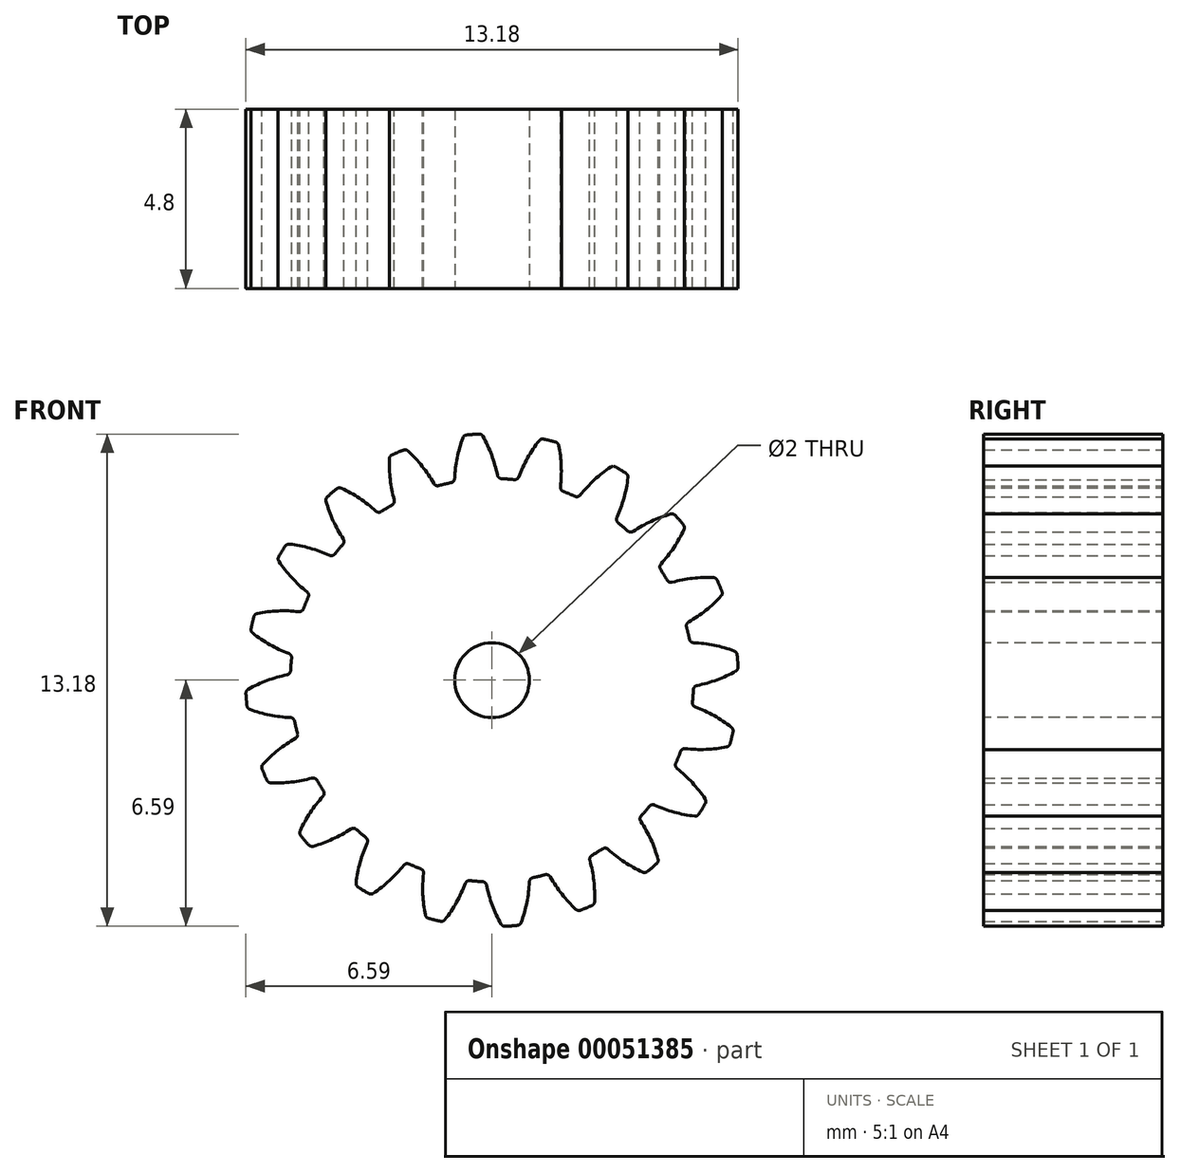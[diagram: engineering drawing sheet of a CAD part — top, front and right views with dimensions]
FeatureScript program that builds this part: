
annotation { "Feature Type Name" : "Feature", "Feature Type Description" : "" }
export const myFeature = defineFeature(function(context is Context, id is Id, definition is map)
    precondition{}
    {
        {
            var Q0;
            Q0=qCreatedBy(makeId("Front.planeOp"),FACE);
            var sketch = newSketch(context, id + "F0", { "sketchPlane" : qUnion([Q0])});
            skCircle(sketch, "E0", {"center": v(0, 0) * mm, "radius": 6 * mm, "construction": true});
            skCircle(sketch, "E1", {"center": v(0, 0) * mm, "radius": 5.4 * mm, "construction": true});
            skCircle(sketch, "E2", {"center": v(0, 0) * mm, "radius": 6.6 * mm, "construction": true});
            skLineSegment(sketch, "E3", {"start": v(0, 0) * mm, "end": v(0, 7.77) * mm, "construction": true});
            skPoint(sketch, "E4", {"position": v(0, 6) * mm});
            skLineSegment(sketch, "E5", {"start": v(0, 6) * mm, "end": v(-7.8, 6) * mm, "construction": true});
            skCircle(sketch, "E6.cCircle", {"center": v(0, 0) * mm, "radius": 7.77 * mm, "construction": true});
            skLineSegment(sketch, "E6.0", {"start": v(-0.61, 7.77) * mm, "end": v(0.61, 7.77) * mm, "construction": true});
            skLineSegment(sketch, "E6.1", {"start": v(0.61, 7.77) * mm, "end": v(1.82, 7.58) * mm, "construction": true});
            skLineSegment(sketch, "E6.2", {"start": v(1.82, 7.58) * mm, "end": v(2.98, 7.2) * mm, "construction": true});
            skLineSegment(sketch, "E6.3", {"start": v(2.98, 7.2) * mm, "end": v(4.07, 6.65) * mm, "construction": true});
            skLineSegment(sketch, "E6.4", {"start": v(4.07, 6.65) * mm, "end": v(5.06, 5.93) * mm, "construction": true});
            skLineSegment(sketch, "E6.5", {"start": v(5.06, 5.93) * mm, "end": v(5.93, 5.06) * mm, "construction": true});
            skLineSegment(sketch, "E6.6", {"start": v(5.93, 5.06) * mm, "end": v(6.65, 4.07) * mm, "construction": true});
            skLineSegment(sketch, "E6.7", {"start": v(6.65, 4.07) * mm, "end": v(7.2, 2.98) * mm, "construction": true});
            skLineSegment(sketch, "E6.8", {"start": v(7.2, 2.98) * mm, "end": v(7.58, 1.82) * mm, "construction": true});
            skLineSegment(sketch, "E6.9", {"start": v(7.58, 1.82) * mm, "end": v(7.77, 0.61) * mm, "construction": true});
            skLineSegment(sketch, "E6.10", {"start": v(7.77, 0.61) * mm, "end": v(7.77, -0.61) * mm, "construction": true});
            skLineSegment(sketch, "E6.11", {"start": v(7.77, -0.61) * mm, "end": v(7.58, -1.82) * mm, "construction": true});
            skLineSegment(sketch, "E6.12", {"start": v(7.58, -1.82) * mm, "end": v(7.2, -2.98) * mm, "construction": true});
            skLineSegment(sketch, "E6.13", {"start": v(7.2, -2.98) * mm, "end": v(6.65, -4.07) * mm, "construction": true});
            skLineSegment(sketch, "E6.14", {"start": v(6.65, -4.07) * mm, "end": v(5.93, -5.06) * mm, "construction": true});
            skLineSegment(sketch, "E6.15", {"start": v(5.93, -5.06) * mm, "end": v(5.06, -5.93) * mm, "construction": true});
            skLineSegment(sketch, "E6.16", {"start": v(5.06, -5.93) * mm, "end": v(4.07, -6.65) * mm, "construction": true});
            skLineSegment(sketch, "E6.17", {"start": v(4.07, -6.65) * mm, "end": v(2.98, -7.2) * mm, "construction": true});
            skLineSegment(sketch, "E6.18", {"start": v(2.98, -7.2) * mm, "end": v(1.82, -7.58) * mm, "construction": true});
            skLineSegment(sketch, "E6.19", {"start": v(1.82, -7.58) * mm, "end": v(0.61, -7.77) * mm, "construction": true});
            skLineSegment(sketch, "E6.20", {"start": v(0.61, -7.77) * mm, "end": v(-0.61, -7.77) * mm, "construction": true});
            skLineSegment(sketch, "E6.21", {"start": v(-0.61, -7.77) * mm, "end": v(-1.82, -7.58) * mm, "construction": true});
            skLineSegment(sketch, "E6.22", {"start": v(-1.82, -7.58) * mm, "end": v(-2.98, -7.2) * mm, "construction": true});
            skLineSegment(sketch, "E6.23", {"start": v(-2.98, -7.2) * mm, "end": v(-4.07, -6.65) * mm, "construction": true});
            skLineSegment(sketch, "E6.24", {"start": v(-4.07, -6.65) * mm, "end": v(-5.06, -5.93) * mm, "construction": true});
            skLineSegment(sketch, "E6.25", {"start": v(-5.06, -5.93) * mm, "end": v(-5.93, -5.06) * mm, "construction": true});
            skLineSegment(sketch, "E6.26", {"start": v(-5.93, -5.06) * mm, "end": v(-6.65, -4.07) * mm, "construction": true});
            skLineSegment(sketch, "E6.27", {"start": v(-6.65, -4.07) * mm, "end": v(-7.2, -2.98) * mm, "construction": true});
            skLineSegment(sketch, "E6.28", {"start": v(-7.2, -2.98) * mm, "end": v(-7.58, -1.82) * mm, "construction": true});
            skLineSegment(sketch, "E6.29", {"start": v(-7.58, -1.82) * mm, "end": v(-7.77, -0.61) * mm, "construction": true});
            skLineSegment(sketch, "E6.30", {"start": v(-7.77, -0.61) * mm, "end": v(-7.77, 0.61) * mm, "construction": true});
            skLineSegment(sketch, "E6.31", {"start": v(-7.77, 0.61) * mm, "end": v(-7.58, 1.82) * mm, "construction": true});
            skLineSegment(sketch, "E6.32", {"start": v(-7.58, 1.82) * mm, "end": v(-7.2, 2.98) * mm, "construction": true});
            skLineSegment(sketch, "E6.33", {"start": v(-7.2, 2.98) * mm, "end": v(-6.65, 4.07) * mm, "construction": true});
            skLineSegment(sketch, "E6.34", {"start": v(-6.65, 4.07) * mm, "end": v(-5.93, 5.06) * mm, "construction": true});
            skLineSegment(sketch, "E6.35", {"start": v(-5.93, 5.06) * mm, "end": v(-5.06, 5.93) * mm, "construction": true});
            skLineSegment(sketch, "E6.36", {"start": v(-5.06, 5.93) * mm, "end": v(-4.07, 6.65) * mm, "construction": true});
            skLineSegment(sketch, "E6.37", {"start": v(-4.07, 6.65) * mm, "end": v(-2.98, 7.2) * mm, "construction": true});
            skLineSegment(sketch, "E6.38", {"start": v(-2.98, 7.2) * mm, "end": v(-1.82, 7.58) * mm, "construction": true});
            skLineSegment(sketch, "E6.39", {"start": v(-1.82, 7.58) * mm, "end": v(-0.61, 7.77) * mm, "construction": true});
            skPoint(sketch, "E6.0.midPoint", {"position": v(0, 7.77) * mm});
            skLineSegment(sketch, "E7.0", {"start": v(0, 7.77) * mm, "end": v(1.22, 7.68) * mm, "construction": true});
            skLineSegment(sketch, "E7.1", {"start": v(1.22, 7.68) * mm, "end": v(2.4, 7.4) * mm, "construction": true});
            skLineSegment(sketch, "E7.2", {"start": v(2.4, 7.4) * mm, "end": v(3.53, 6.93) * mm, "construction": true});
            skLineSegment(sketch, "E7.3", {"start": v(3.53, 6.93) * mm, "end": v(4.57, 6.29) * mm, "construction": true});
            skLineSegment(sketch, "E7.4", {"start": v(4.57, 6.29) * mm, "end": v(5.5, 5.5) * mm, "construction": true});
            skLineSegment(sketch, "E7.5", {"start": v(5.5, 5.5) * mm, "end": v(6.29, 4.57) * mm, "construction": true});
            skLineSegment(sketch, "E7.6", {"start": v(6.29, 4.57) * mm, "end": v(6.93, 3.53) * mm, "construction": true});
            skLineSegment(sketch, "E7.7", {"start": v(6.93, 3.53) * mm, "end": v(7.4, 2.4) * mm, "construction": true});
            skLineSegment(sketch, "E7.8", {"start": v(7.4, 2.4) * mm, "end": v(7.68, 1.22) * mm, "construction": true});
            skLineSegment(sketch, "E7.9", {"start": v(7.68, 1.22) * mm, "end": v(7.77, 0) * mm, "construction": true});
            skLineSegment(sketch, "E7.10", {"start": v(7.77, 0) * mm, "end": v(7.68, -1.22) * mm, "construction": true});
            skLineSegment(sketch, "E7.11", {"start": v(7.68, -1.22) * mm, "end": v(7.4, -2.4) * mm, "construction": true});
            skLineSegment(sketch, "E7.12", {"start": v(7.4, -2.4) * mm, "end": v(6.93, -3.53) * mm, "construction": true});
            skLineSegment(sketch, "E7.13", {"start": v(6.93, -3.53) * mm, "end": v(6.29, -4.57) * mm, "construction": true});
            skLineSegment(sketch, "E7.14", {"start": v(6.29, -4.57) * mm, "end": v(5.5, -5.5) * mm, "construction": true});
            skLineSegment(sketch, "E7.15", {"start": v(5.5, -5.5) * mm, "end": v(4.57, -6.29) * mm, "construction": true});
            skLineSegment(sketch, "E7.16", {"start": v(4.57, -6.29) * mm, "end": v(3.53, -6.93) * mm, "construction": true});
            skLineSegment(sketch, "E7.17", {"start": v(3.53, -6.93) * mm, "end": v(2.4, -7.4) * mm, "construction": true});
            skLineSegment(sketch, "E7.18", {"start": v(2.4, -7.4) * mm, "end": v(1.22, -7.68) * mm, "construction": true});
            skLineSegment(sketch, "E7.19", {"start": v(1.22, -7.68) * mm, "end": v(0, -7.77) * mm, "construction": true});
            skLineSegment(sketch, "E7.20", {"start": v(0, -7.77) * mm, "end": v(-1.22, -7.68) * mm, "construction": true});
            skLineSegment(sketch, "E7.21", {"start": v(-1.22, -7.68) * mm, "end": v(-2.4, -7.4) * mm, "construction": true});
            skLineSegment(sketch, "E7.22", {"start": v(-2.4, -7.4) * mm, "end": v(-3.53, -6.93) * mm, "construction": true});
            skLineSegment(sketch, "E7.23", {"start": v(-3.53, -6.93) * mm, "end": v(-4.57, -6.29) * mm, "construction": true});
            skLineSegment(sketch, "E7.24", {"start": v(-4.57, -6.29) * mm, "end": v(-5.5, -5.5) * mm, "construction": true});
            skLineSegment(sketch, "E7.25", {"start": v(-5.5, -5.5) * mm, "end": v(-6.29, -4.57) * mm, "construction": true});
            skLineSegment(sketch, "E7.26", {"start": v(-6.29, -4.57) * mm, "end": v(-6.93, -3.53) * mm, "construction": true});
            skLineSegment(sketch, "E7.27", {"start": v(-6.93, -3.53) * mm, "end": v(-7.4, -2.4) * mm, "construction": true});
            skLineSegment(sketch, "E7.28", {"start": v(-7.4, -2.4) * mm, "end": v(-7.68, -1.22) * mm, "construction": true});
            skLineSegment(sketch, "E7.29", {"start": v(-7.68, -1.22) * mm, "end": v(-7.77, 0) * mm, "construction": true});
            skLineSegment(sketch, "E7.30", {"start": v(-7.77, 0) * mm, "end": v(-7.68, 1.22) * mm, "construction": true});
            skLineSegment(sketch, "E7.31", {"start": v(-7.68, 1.22) * mm, "end": v(-7.4, 2.4) * mm, "construction": true});
            skLineSegment(sketch, "E7.32", {"start": v(-7.4, 2.4) * mm, "end": v(-6.93, 3.53) * mm, "construction": true});
            skLineSegment(sketch, "E7.33", {"start": v(-6.93, 3.53) * mm, "end": v(-6.29, 4.57) * mm, "construction": true});
            skLineSegment(sketch, "E7.34", {"start": v(-6.29, 4.57) * mm, "end": v(-5.5, 5.5) * mm, "construction": true});
            skLineSegment(sketch, "E7.35", {"start": v(-5.5, 5.5) * mm, "end": v(-4.57, 6.29) * mm, "construction": true});
            skLineSegment(sketch, "E7.36", {"start": v(-4.57, 6.29) * mm, "end": v(-3.53, 6.93) * mm, "construction": true});
            skLineSegment(sketch, "E7.37", {"start": v(-3.53, 6.93) * mm, "end": v(-2.4, 7.4) * mm, "construction": true});
            skLineSegment(sketch, "E7.38", {"start": v(-2.4, 7.4) * mm, "end": v(-1.22, 7.68) * mm, "construction": true});
            skLineSegment(sketch, "E7.39", {"start": v(-1.22, 7.68) * mm, "end": v(0, 7.77) * mm, "construction": true});
            skLineSegment(sketch, "E8", {"start": v(0, 0) * mm, "end": v(-0.61, 7.77) * mm, "construction": true});
            skLineSegment(sketch, "E9", {"start": v(0, 6) * mm, "end": v(-7.35, 3.32) * mm, "construction": true});
            skCircle(sketch, "E10", {"center": v(0, 6) * mm, "radius": 3.6 * mm, "construction": true});
            skPoint(sketch, "E11", {"position": v(-3.38, 4.77) * mm});
            skCircle(sketch, "E12", {"center": v(-3.38, 4.77) * mm, "radius": 3.6 * mm, "construction": true});
            skArc(sketch, "E13", {"start": v(-0.24, 6.53) * mm, "mid": v(0, 6.02) * mm, "end": v(0.14, 5.49) * mm});
            skArc(sketch, "E14.MirrorCS", {"start": v(-0.78, 6.49) * mm, "mid": v(-0.93, 5.95) * mm, "end": v(-1, 5.4) * mm});
            skArc(sketch, "E15", {"start": v(-0.68, 6.56) * mm, "mid": v(-0.52, 6.58) * mm, "end": v(-0.35, 6.6) * mm});
            skArc(sketch, "E16", {"start": v(-1.1, 5.29) * mm, "mid": v(0.42, -5.38) * mm, "end": v(0.26, 5.4) * mm});
            skPoint(sketch, "E17.visualSharp", {"position": v(-1, 5.3) * mm});
            skArc(sketch, "E17.filletArc", {"start": v(-1.1, 5.29) * mm, "mid": v(-1.03, 5.33) * mm, "end": v(-1, 5.4) * mm});
            skPoint(sketch, "E18.visualSharp", {"position": v(0.16, 5.4) * mm});
            skArc(sketch, "E18.filletArc", {"start": v(0.14, 5.49) * mm, "mid": v(0.18, 5.42) * mm, "end": v(0.26, 5.4) * mm});
            skPoint(sketch, "E19.visualSharp", {"position": v(-0.76, 6.56) * mm});
            skArc(sketch, "E19.filletArc", {"start": v(-0.68, 6.56) * mm, "mid": v(-0.74, 6.54) * mm, "end": v(-0.78, 6.49) * mm});
            skPoint(sketch, "E20.visualSharp", {"position": v(-0.28, 6.6) * mm});
            skArc(sketch, "E20.filletArc", {"start": v(-0.24, 6.53) * mm, "mid": v(-0.29, 6.58) * mm, "end": v(-0.35, 6.6) * mm});
            skLineSegment(sketch, "E21", {"start": v(0, 0) * mm, "end": v(-1.44, 6.92) * mm, "construction": true});
            skPoint(sketch, "E22.1.0", {"position": v(-1.51, 5.18) * mm});
            skPoint(sketch, "E22.1.1", {"position": v(-1.85, 5.7) * mm});
            skArc(sketch, "E22.1.2", {"start": v(-2.25, 6.13) * mm, "mid": v(-1.87, 5.73) * mm, "end": v(-1.56, 5.27) * mm});
            skArc(sketch, "E22.1.3", {"start": v(-2.68, 6.03) * mm, "mid": v(-2.53, 6.1) * mm, "end": v(-2.37, 6.16) * mm});
            skPoint(sketch, "E22.1.4", {"position": v(-2.3, 6.18) * mm});
            skPoint(sketch, "E22.1.5", {"position": v(-2.6, 4.74) * mm});
            skArc(sketch, "E22.1.6", {"start": v(-2.75, 5.93) * mm, "mid": v(-2.73, 5.37) * mm, "end": v(-2.62, 4.83) * mm});
            skPoint(sketch, "E22.1.7", {"position": v(-2.74, 6) * mm});
            skArc(sketch, "E22.1.8", {"start": v(-1.56, 5.27) * mm, "mid": v(-1.5, 5.21) * mm, "end": v(-1.42, 5.2) * mm});
            skArc(sketch, "E22.1.9", {"start": v(-2.68, 6.03) * mm, "mid": v(-2.73, 6) * mm, "end": v(-2.75, 5.93) * mm});
            skArc(sketch, "E22.1.10", {"start": v(-2.68, 4.69) * mm, "mid": v(-2.63, 4.75) * mm, "end": v(-2.62, 4.83) * mm});
            skArc(sketch, "E22.1.11", {"start": v(-2.25, 6.13) * mm, "mid": v(-2.3, 6.16) * mm, "end": v(-2.37, 6.16) * mm});
            skPoint(sketch, "E22.2.0", {"position": v(-3.04, 4.46) * mm});
            skPoint(sketch, "E22.2.1", {"position": v(-3.53, 4.85) * mm});
            skArc(sketch, "E22.2.2", {"start": v(-4.03, 5.14) * mm, "mid": v(-3.55, 4.87) * mm, "end": v(-3.11, 4.53) * mm});
            skArc(sketch, "E22.2.3", {"start": v(-4.4, 4.91) * mm, "mid": v(-4.29, 5.02) * mm, "end": v(-4.16, 5.12) * mm});
            skPoint(sketch, "E22.2.4", {"position": v(-4.1, 5.17) * mm});
            skPoint(sketch, "E22.2.5", {"position": v(-3.93, 3.7) * mm});
            skArc(sketch, "E22.2.6", {"start": v(-4.45, 4.79) * mm, "mid": v(-4.25, 4.27) * mm, "end": v(-3.98, 3.78) * mm});
            skPoint(sketch, "E22.2.7", {"position": v(-4.46, 4.86) * mm});
            skArc(sketch, "E22.2.8", {"start": v(-3.11, 4.53) * mm, "mid": v(-3.04, 4.5) * mm, "end": v(-2.96, 4.51) * mm});
            skArc(sketch, "E22.2.9", {"start": v(-4.4, 4.91) * mm, "mid": v(-4.45, 4.85) * mm, "end": v(-4.45, 4.79) * mm});
            skArc(sketch, "E22.2.10", {"start": v(-4, 3.63) * mm, "mid": v(-3.96, 3.7) * mm, "end": v(-3.98, 3.78) * mm});
            skArc(sketch, "E22.2.11", {"start": v(-4.03, 5.14) * mm, "mid": v(-4.1, 5.15) * mm, "end": v(-4.16, 5.12) * mm});
            skPoint(sketch, "E22.3.0", {"position": v(-4.27, 3.3) * mm});
            skPoint(sketch, "E22.3.1", {"position": v(-4.85, 3.53) * mm});
            skArc(sketch, "E22.3.2", {"start": v(-5.43, 3.64) * mm, "mid": v(-4.88, 3.53) * mm, "end": v(-4.36, 3.34) * mm});
            skArc(sketch, "E22.3.3", {"start": v(-5.71, 3.3) * mm, "mid": v(-5.63, 3.45) * mm, "end": v(-5.54, 3.59) * mm});
            skPoint(sketch, "E22.3.4", {"position": v(-5.5, 3.65) * mm});
            skPoint(sketch, "E22.3.5", {"position": v(-4.88, 2.3) * mm});
            skArc(sketch, "E22.3.6", {"start": v(-5.7, 3.18) * mm, "mid": v(-5.36, 2.74) * mm, "end": v(-4.96, 2.36) * mm});
            skPoint(sketch, "E22.3.7", {"position": v(-5.75, 3.24) * mm});
            skArc(sketch, "E22.3.8", {"start": v(-4.36, 3.34) * mm, "mid": v(-4.28, 3.34) * mm, "end": v(-4.21, 3.38) * mm});
            skArc(sketch, "E22.3.9", {"start": v(-5.71, 3.3) * mm, "mid": v(-5.73, 3.24) * mm, "end": v(-5.7, 3.18) * mm});
            skArc(sketch, "E22.3.10", {"start": v(-4.92, 2.22) * mm, "mid": v(-4.92, 2.3) * mm, "end": v(-4.96, 2.36) * mm});
            skArc(sketch, "E22.3.11", {"start": v(-5.43, 3.64) * mm, "mid": v(-5.5, 3.63) * mm, "end": v(-5.54, 3.59) * mm});
            skPoint(sketch, "E22.4.0", {"position": v(-5.08, 1.82) * mm});
            skPoint(sketch, "E22.4.1", {"position": v(-5.7, 1.85) * mm});
            skArc(sketch, "E22.4.2", {"start": v(-6.28, 1.79) * mm, "mid": v(-5.73, 1.85) * mm, "end": v(-5.18, 1.83) * mm});
            skArc(sketch, "E22.4.3", {"start": v(-6.45, 1.38) * mm, "mid": v(-6.42, 1.54) * mm, "end": v(-6.38, 1.7) * mm});
            skPoint(sketch, "E22.4.4", {"position": v(-6.36, 1.77) * mm});
            skPoint(sketch, "E22.4.5", {"position": v(-5.36, 0.68) * mm});
            skArc(sketch, "E22.4.6", {"start": v(-6.41, 1.26) * mm, "mid": v(-5.95, 0.95) * mm, "end": v(-5.44, 0.72) * mm});
            skPoint(sketch, "E22.4.7", {"position": v(-6.47, 1.3) * mm});
            skArc(sketch, "E22.4.8", {"start": v(-5.18, 1.83) * mm, "mid": v(-5.1, 1.85) * mm, "end": v(-5.05, 1.91) * mm});
            skArc(sketch, "E22.4.9", {"start": v(-6.45, 1.38) * mm, "mid": v(-6.45, 1.31) * mm, "end": v(-6.41, 1.26) * mm});
            skArc(sketch, "E22.4.10", {"start": v(-5.37, 0.6) * mm, "mid": v(-5.38, 0.67) * mm, "end": v(-5.44, 0.72) * mm});
            skArc(sketch, "E22.4.11", {"start": v(-6.28, 1.79) * mm, "mid": v(-6.34, 1.76) * mm, "end": v(-6.38, 1.7) * mm});
            skPoint(sketch, "E22.5.0", {"position": v(-5.4, 0.16) * mm});
            skPoint(sketch, "E22.5.1", {"position": v(-6, 0) * mm});
            skArc(sketch, "E22.5.2", {"start": v(-6.53, -0.24) * mm, "mid": v(-6.02, 0) * mm, "end": v(-5.49, 0.14) * mm});
            skArc(sketch, "E22.5.3", {"start": v(-6.56, -0.68) * mm, "mid": v(-6.58, -0.52) * mm, "end": v(-6.6, -0.35) * mm});
            skPoint(sketch, "E22.5.4", {"position": v(-6.6, -0.28) * mm});
            skPoint(sketch, "E22.5.5", {"position": v(-5.3, -1) * mm});
            skArc(sketch, "E22.5.6", {"start": v(-6.49, -0.78) * mm, "mid": v(-5.95, -0.93) * mm, "end": v(-5.4, -1) * mm});
            skPoint(sketch, "E22.5.7", {"position": v(-6.56, -0.76) * mm});
            skArc(sketch, "E22.5.8", {"start": v(-5.49, 0.14) * mm, "mid": v(-5.42, 0.18) * mm, "end": v(-5.4, 0.26) * mm});
            skArc(sketch, "E22.5.9", {"start": v(-6.56, -0.68) * mm, "mid": v(-6.54, -0.74) * mm, "end": v(-6.49, -0.78) * mm});
            skArc(sketch, "E22.5.10", {"start": v(-5.29, -1.1) * mm, "mid": v(-5.33, -1.03) * mm, "end": v(-5.4, -1) * mm});
            skArc(sketch, "E22.5.11", {"start": v(-6.53, -0.24) * mm, "mid": v(-6.58, -0.29) * mm, "end": v(-6.6, -0.35) * mm});
            skPoint(sketch, "E22.6.0", {"position": v(-5.18, -1.51) * mm});
            skPoint(sketch, "E22.6.1", {"position": v(-5.7, -1.85) * mm});
            skArc(sketch, "E22.6.2", {"start": v(-6.13, -2.25) * mm, "mid": v(-5.73, -1.87) * mm, "end": v(-5.27, -1.56) * mm});
            skArc(sketch, "E22.6.3", {"start": v(-6.03, -2.68) * mm, "mid": v(-6.1, -2.53) * mm, "end": v(-6.16, -2.37) * mm});
            skPoint(sketch, "E22.6.4", {"position": v(-6.18, -2.3) * mm});
            skPoint(sketch, "E22.6.5", {"position": v(-4.74, -2.6) * mm});
            skArc(sketch, "E22.6.6", {"start": v(-5.93, -2.75) * mm, "mid": v(-5.37, -2.73) * mm, "end": v(-4.83, -2.62) * mm});
            skPoint(sketch, "E22.6.7", {"position": v(-6, -2.74) * mm});
            skArc(sketch, "E22.6.8", {"start": v(-5.27, -1.56) * mm, "mid": v(-5.21, -1.5) * mm, "end": v(-5.2, -1.42) * mm});
            skArc(sketch, "E22.6.9", {"start": v(-6.03, -2.68) * mm, "mid": v(-6, -2.73) * mm, "end": v(-5.93, -2.75) * mm});
            skArc(sketch, "E22.6.10", {"start": v(-4.69, -2.68) * mm, "mid": v(-4.75, -2.63) * mm, "end": v(-4.83, -2.62) * mm});
            skArc(sketch, "E22.6.11", {"start": v(-6.13, -2.25) * mm, "mid": v(-6.16, -2.3) * mm, "end": v(-6.16, -2.37) * mm});
            skPoint(sketch, "E22.7.0", {"position": v(-4.46, -3.04) * mm});
            skPoint(sketch, "E22.7.1", {"position": v(-4.85, -3.53) * mm});
            skArc(sketch, "E22.7.2", {"start": v(-5.14, -4.03) * mm, "mid": v(-4.87, -3.55) * mm, "end": v(-4.53, -3.11) * mm});
            skArc(sketch, "E22.7.3", {"start": v(-4.91, -4.4) * mm, "mid": v(-5.02, -4.29) * mm, "end": v(-5.12, -4.16) * mm});
            skPoint(sketch, "E22.7.4", {"position": v(-5.17, -4.1) * mm});
            skPoint(sketch, "E22.7.5", {"position": v(-3.7, -3.93) * mm});
            skArc(sketch, "E22.7.6", {"start": v(-4.79, -4.45) * mm, "mid": v(-4.27, -4.25) * mm, "end": v(-3.78, -3.98) * mm});
            skPoint(sketch, "E22.7.7", {"position": v(-4.86, -4.46) * mm});
            skArc(sketch, "E22.7.8", {"start": v(-4.53, -3.11) * mm, "mid": v(-4.5, -3.04) * mm, "end": v(-4.51, -2.96) * mm});
            skArc(sketch, "E22.7.9", {"start": v(-4.91, -4.4) * mm, "mid": v(-4.85, -4.45) * mm, "end": v(-4.79, -4.45) * mm});
            skArc(sketch, "E22.7.10", {"start": v(-3.63, -4) * mm, "mid": v(-3.7, -3.96) * mm, "end": v(-3.78, -3.98) * mm});
            skArc(sketch, "E22.7.11", {"start": v(-5.14, -4.03) * mm, "mid": v(-5.15, -4.1) * mm, "end": v(-5.12, -4.16) * mm});
            skPoint(sketch, "E22.8.0", {"position": v(-3.3, -4.27) * mm});
            skPoint(sketch, "E22.8.1", {"position": v(-3.53, -4.85) * mm});
            skArc(sketch, "E22.8.2", {"start": v(-3.64, -5.43) * mm, "mid": v(-3.53, -4.88) * mm, "end": v(-3.34, -4.36) * mm});
            skArc(sketch, "E22.8.3", {"start": v(-3.3, -5.71) * mm, "mid": v(-3.45, -5.63) * mm, "end": v(-3.59, -5.54) * mm});
            skPoint(sketch, "E22.8.4", {"position": v(-3.65, -5.5) * mm});
            skPoint(sketch, "E22.8.5", {"position": v(-2.3, -4.88) * mm});
            skArc(sketch, "E22.8.6", {"start": v(-3.18, -5.7) * mm, "mid": v(-2.74, -5.36) * mm, "end": v(-2.36, -4.96) * mm});
            skPoint(sketch, "E22.8.7", {"position": v(-3.24, -5.75) * mm});
            skArc(sketch, "E22.8.8", {"start": v(-3.34, -4.36) * mm, "mid": v(-3.34, -4.28) * mm, "end": v(-3.38, -4.21) * mm});
            skArc(sketch, "E22.8.9", {"start": v(-3.3, -5.71) * mm, "mid": v(-3.24, -5.73) * mm, "end": v(-3.18, -5.7) * mm});
            skArc(sketch, "E22.8.10", {"start": v(-2.22, -4.92) * mm, "mid": v(-2.3, -4.92) * mm, "end": v(-2.36, -4.96) * mm});
            skArc(sketch, "E22.8.11", {"start": v(-3.64, -5.43) * mm, "mid": v(-3.63, -5.5) * mm, "end": v(-3.59, -5.54) * mm});
            skPoint(sketch, "E22.9.0", {"position": v(-1.82, -5.08) * mm});
            skPoint(sketch, "E22.9.1", {"position": v(-1.85, -5.7) * mm});
            skArc(sketch, "E22.9.2", {"start": v(-1.79, -6.28) * mm, "mid": v(-1.85, -5.73) * mm, "end": v(-1.83, -5.18) * mm});
            skArc(sketch, "E22.9.3", {"start": v(-1.38, -6.45) * mm, "mid": v(-1.54, -6.42) * mm, "end": v(-1.7, -6.38) * mm});
            skPoint(sketch, "E22.9.4", {"position": v(-1.77, -6.36) * mm});
            skPoint(sketch, "E22.9.5", {"position": v(-0.68, -5.36) * mm});
            skArc(sketch, "E22.9.6", {"start": v(-1.26, -6.41) * mm, "mid": v(-0.95, -5.95) * mm, "end": v(-0.72, -5.44) * mm});
            skPoint(sketch, "E22.9.7", {"position": v(-1.3, -6.47) * mm});
            skArc(sketch, "E22.9.8", {"start": v(-1.83, -5.18) * mm, "mid": v(-1.85, -5.1) * mm, "end": v(-1.91, -5.05) * mm});
            skArc(sketch, "E22.9.9", {"start": v(-1.38, -6.45) * mm, "mid": v(-1.31, -6.45) * mm, "end": v(-1.26, -6.41) * mm});
            skArc(sketch, "E22.9.10", {"start": v(-0.6, -5.37) * mm, "mid": v(-0.67, -5.38) * mm, "end": v(-0.72, -5.44) * mm});
            skArc(sketch, "E22.9.11", {"start": v(-1.79, -6.28) * mm, "mid": v(-1.76, -6.34) * mm, "end": v(-1.7, -6.38) * mm});
            skPoint(sketch, "E22.10.0", {"position": v(-0.16, -5.4) * mm});
            skPoint(sketch, "E22.10.1", {"position": v(0, -6) * mm});
            skArc(sketch, "E22.10.2", {"start": v(0.24, -6.53) * mm, "mid": v(0, -6.02) * mm, "end": v(-0.14, -5.49) * mm});
            skArc(sketch, "E22.10.3", {"start": v(0.68, -6.56) * mm, "mid": v(0.52, -6.58) * mm, "end": v(0.35, -6.6) * mm});
            skPoint(sketch, "E22.10.4", {"position": v(0.28, -6.6) * mm});
            skPoint(sketch, "E22.10.5", {"position": v(1, -5.3) * mm});
            skArc(sketch, "E22.10.6", {"start": v(0.78, -6.49) * mm, "mid": v(0.93, -5.95) * mm, "end": v(1, -5.4) * mm});
            skPoint(sketch, "E22.10.7", {"position": v(0.76, -6.56) * mm});
            skArc(sketch, "E22.10.8", {"start": v(-0.14, -5.49) * mm, "mid": v(-0.18, -5.42) * mm, "end": v(-0.26, -5.4) * mm});
            skArc(sketch, "E22.10.9", {"start": v(0.68, -6.56) * mm, "mid": v(0.74, -6.54) * mm, "end": v(0.78, -6.49) * mm});
            skArc(sketch, "E22.10.10", {"start": v(1.1, -5.29) * mm, "mid": v(1.03, -5.33) * mm, "end": v(1, -5.4) * mm});
            skArc(sketch, "E22.10.11", {"start": v(0.24, -6.53) * mm, "mid": v(0.29, -6.58) * mm, "end": v(0.35, -6.6) * mm});
            skPoint(sketch, "E22.11.0", {"position": v(1.51, -5.18) * mm});
            skPoint(sketch, "E22.11.1", {"position": v(1.85, -5.7) * mm});
            skArc(sketch, "E22.11.2", {"start": v(2.25, -6.13) * mm, "mid": v(1.87, -5.73) * mm, "end": v(1.56, -5.27) * mm});
            skArc(sketch, "E22.11.3", {"start": v(2.68, -6.03) * mm, "mid": v(2.53, -6.1) * mm, "end": v(2.37, -6.16) * mm});
            skPoint(sketch, "E22.11.4", {"position": v(2.3, -6.18) * mm});
            skPoint(sketch, "E22.11.5", {"position": v(2.6, -4.74) * mm});
            skArc(sketch, "E22.11.6", {"start": v(2.75, -5.93) * mm, "mid": v(2.73, -5.37) * mm, "end": v(2.62, -4.83) * mm});
            skPoint(sketch, "E22.11.7", {"position": v(2.74, -6) * mm});
            skArc(sketch, "E22.11.8", {"start": v(1.56, -5.27) * mm, "mid": v(1.5, -5.21) * mm, "end": v(1.42, -5.2) * mm});
            skArc(sketch, "E22.11.9", {"start": v(2.68, -6.03) * mm, "mid": v(2.73, -6) * mm, "end": v(2.75, -5.93) * mm});
            skArc(sketch, "E22.11.10", {"start": v(2.68, -4.69) * mm, "mid": v(2.63, -4.75) * mm, "end": v(2.62, -4.83) * mm});
            skArc(sketch, "E22.11.11", {"start": v(2.25, -6.13) * mm, "mid": v(2.3, -6.16) * mm, "end": v(2.37, -6.16) * mm});
            skPoint(sketch, "E22.12.0", {"position": v(3.04, -4.46) * mm});
            skPoint(sketch, "E22.12.1", {"position": v(3.53, -4.85) * mm});
            skArc(sketch, "E22.12.2", {"start": v(4.03, -5.14) * mm, "mid": v(3.55, -4.87) * mm, "end": v(3.11, -4.53) * mm});
            skArc(sketch, "E22.12.3", {"start": v(4.4, -4.91) * mm, "mid": v(4.29, -5.02) * mm, "end": v(4.16, -5.12) * mm});
            skPoint(sketch, "E22.12.4", {"position": v(4.1, -5.17) * mm});
            skPoint(sketch, "E22.12.5", {"position": v(3.93, -3.7) * mm});
            skArc(sketch, "E22.12.6", {"start": v(4.45, -4.79) * mm, "mid": v(4.25, -4.27) * mm, "end": v(3.98, -3.78) * mm});
            skPoint(sketch, "E22.12.7", {"position": v(4.46, -4.86) * mm});
            skArc(sketch, "E22.12.8", {"start": v(3.11, -4.53) * mm, "mid": v(3.04, -4.5) * mm, "end": v(2.96, -4.51) * mm});
            skArc(sketch, "E22.12.9", {"start": v(4.4, -4.91) * mm, "mid": v(4.45, -4.85) * mm, "end": v(4.45, -4.79) * mm});
            skArc(sketch, "E22.12.10", {"start": v(4, -3.63) * mm, "mid": v(3.96, -3.7) * mm, "end": v(3.98, -3.78) * mm});
            skArc(sketch, "E22.12.11", {"start": v(4.03, -5.14) * mm, "mid": v(4.1, -5.15) * mm, "end": v(4.16, -5.12) * mm});
            skPoint(sketch, "E22.13.0", {"position": v(4.27, -3.3) * mm});
            skPoint(sketch, "E22.13.1", {"position": v(4.85, -3.53) * mm});
            skArc(sketch, "E22.13.2", {"start": v(5.43, -3.64) * mm, "mid": v(4.88, -3.53) * mm, "end": v(4.36, -3.34) * mm});
            skArc(sketch, "E22.13.3", {"start": v(5.71, -3.3) * mm, "mid": v(5.63, -3.45) * mm, "end": v(5.54, -3.59) * mm});
            skPoint(sketch, "E22.13.4", {"position": v(5.5, -3.65) * mm});
            skPoint(sketch, "E22.13.5", {"position": v(4.88, -2.3) * mm});
            skArc(sketch, "E22.13.6", {"start": v(5.7, -3.18) * mm, "mid": v(5.36, -2.74) * mm, "end": v(4.96, -2.36) * mm});
            skPoint(sketch, "E22.13.7", {"position": v(5.75, -3.24) * mm});
            skArc(sketch, "E22.13.8", {"start": v(4.36, -3.34) * mm, "mid": v(4.28, -3.34) * mm, "end": v(4.21, -3.38) * mm});
            skArc(sketch, "E22.13.9", {"start": v(5.71, -3.3) * mm, "mid": v(5.73, -3.24) * mm, "end": v(5.7, -3.18) * mm});
            skArc(sketch, "E22.13.10", {"start": v(4.92, -2.22) * mm, "mid": v(4.92, -2.3) * mm, "end": v(4.96, -2.36) * mm});
            skArc(sketch, "E22.13.11", {"start": v(5.43, -3.64) * mm, "mid": v(5.5, -3.63) * mm, "end": v(5.54, -3.59) * mm});
            skPoint(sketch, "E22.14.0", {"position": v(5.08, -1.82) * mm});
            skPoint(sketch, "E22.14.1", {"position": v(5.7, -1.85) * mm});
            skArc(sketch, "E22.14.2", {"start": v(6.28, -1.79) * mm, "mid": v(5.73, -1.85) * mm, "end": v(5.18, -1.83) * mm});
            skArc(sketch, "E22.14.3", {"start": v(6.45, -1.38) * mm, "mid": v(6.42, -1.54) * mm, "end": v(6.38, -1.7) * mm});
            skPoint(sketch, "E22.14.4", {"position": v(6.36, -1.77) * mm});
            skPoint(sketch, "E22.14.5", {"position": v(5.36, -0.68) * mm});
            skArc(sketch, "E22.14.6", {"start": v(6.41, -1.26) * mm, "mid": v(5.95, -0.95) * mm, "end": v(5.44, -0.72) * mm});
            skPoint(sketch, "E22.14.7", {"position": v(6.47, -1.3) * mm});
            skArc(sketch, "E22.14.8", {"start": v(5.18, -1.83) * mm, "mid": v(5.1, -1.85) * mm, "end": v(5.05, -1.91) * mm});
            skArc(sketch, "E22.14.9", {"start": v(6.45, -1.38) * mm, "mid": v(6.45, -1.31) * mm, "end": v(6.41, -1.26) * mm});
            skArc(sketch, "E22.14.10", {"start": v(5.37, -0.6) * mm, "mid": v(5.38, -0.67) * mm, "end": v(5.44, -0.72) * mm});
            skArc(sketch, "E22.14.11", {"start": v(6.28, -1.79) * mm, "mid": v(6.34, -1.76) * mm, "end": v(6.38, -1.7) * mm});
            skPoint(sketch, "E22.15.0", {"position": v(5.4, -0.16) * mm});
            skPoint(sketch, "E22.15.1", {"position": v(6, 0) * mm});
            skArc(sketch, "E22.15.2", {"start": v(6.53, 0.24) * mm, "mid": v(6.02, 0) * mm, "end": v(5.49, -0.14) * mm});
            skArc(sketch, "E22.15.3", {"start": v(6.56, 0.68) * mm, "mid": v(6.58, 0.52) * mm, "end": v(6.6, 0.35) * mm});
            skPoint(sketch, "E22.15.4", {"position": v(6.6, 0.28) * mm});
            skPoint(sketch, "E22.15.5", {"position": v(5.3, 1) * mm});
            skArc(sketch, "E22.15.6", {"start": v(6.49, 0.78) * mm, "mid": v(5.95, 0.93) * mm, "end": v(5.4, 1) * mm});
            skPoint(sketch, "E22.15.7", {"position": v(6.56, 0.76) * mm});
            skArc(sketch, "E22.15.8", {"start": v(5.49, -0.14) * mm, "mid": v(5.42, -0.18) * mm, "end": v(5.4, -0.26) * mm});
            skArc(sketch, "E22.15.9", {"start": v(6.56, 0.68) * mm, "mid": v(6.54, 0.74) * mm, "end": v(6.49, 0.78) * mm});
            skArc(sketch, "E22.15.10", {"start": v(5.29, 1.1) * mm, "mid": v(5.33, 1.03) * mm, "end": v(5.4, 1) * mm});
            skArc(sketch, "E22.15.11", {"start": v(6.53, 0.24) * mm, "mid": v(6.58, 0.29) * mm, "end": v(6.6, 0.35) * mm});
            skPoint(sketch, "E22.16.0", {"position": v(5.18, 1.51) * mm});
            skPoint(sketch, "E22.16.1", {"position": v(5.7, 1.85) * mm});
            skArc(sketch, "E22.16.2", {"start": v(6.13, 2.25) * mm, "mid": v(5.73, 1.87) * mm, "end": v(5.27, 1.56) * mm});
            skArc(sketch, "E22.16.3", {"start": v(6.03, 2.68) * mm, "mid": v(6.1, 2.53) * mm, "end": v(6.16, 2.37) * mm});
            skPoint(sketch, "E22.16.4", {"position": v(6.18, 2.3) * mm});
            skPoint(sketch, "E22.16.5", {"position": v(4.74, 2.6) * mm});
            skArc(sketch, "E22.16.6", {"start": v(5.93, 2.75) * mm, "mid": v(5.37, 2.73) * mm, "end": v(4.83, 2.62) * mm});
            skPoint(sketch, "E22.16.7", {"position": v(6, 2.74) * mm});
            skArc(sketch, "E22.16.8", {"start": v(5.27, 1.56) * mm, "mid": v(5.21, 1.5) * mm, "end": v(5.2, 1.42) * mm});
            skArc(sketch, "E22.16.9", {"start": v(6.03, 2.68) * mm, "mid": v(6, 2.73) * mm, "end": v(5.93, 2.75) * mm});
            skArc(sketch, "E22.16.10", {"start": v(4.69, 2.68) * mm, "mid": v(4.75, 2.63) * mm, "end": v(4.83, 2.62) * mm});
            skArc(sketch, "E22.16.11", {"start": v(6.13, 2.25) * mm, "mid": v(6.16, 2.3) * mm, "end": v(6.16, 2.37) * mm});
            skPoint(sketch, "E22.17.0", {"position": v(4.46, 3.04) * mm});
            skPoint(sketch, "E22.17.1", {"position": v(4.85, 3.53) * mm});
            skArc(sketch, "E22.17.2", {"start": v(5.14, 4.03) * mm, "mid": v(4.87, 3.55) * mm, "end": v(4.53, 3.11) * mm});
            skArc(sketch, "E22.17.3", {"start": v(4.91, 4.4) * mm, "mid": v(5.02, 4.29) * mm, "end": v(5.12, 4.16) * mm});
            skPoint(sketch, "E22.17.4", {"position": v(5.17, 4.1) * mm});
            skPoint(sketch, "E22.17.5", {"position": v(3.7, 3.93) * mm});
            skArc(sketch, "E22.17.6", {"start": v(4.79, 4.45) * mm, "mid": v(4.27, 4.25) * mm, "end": v(3.78, 3.98) * mm});
            skPoint(sketch, "E22.17.7", {"position": v(4.86, 4.46) * mm});
            skArc(sketch, "E22.17.8", {"start": v(4.53, 3.11) * mm, "mid": v(4.5, 3.04) * mm, "end": v(4.51, 2.96) * mm});
            skArc(sketch, "E22.17.9", {"start": v(4.91, 4.4) * mm, "mid": v(4.85, 4.45) * mm, "end": v(4.79, 4.45) * mm});
            skArc(sketch, "E22.17.10", {"start": v(3.63, 4) * mm, "mid": v(3.7, 3.96) * mm, "end": v(3.78, 3.98) * mm});
            skArc(sketch, "E22.17.11", {"start": v(5.14, 4.03) * mm, "mid": v(5.15, 4.1) * mm, "end": v(5.12, 4.16) * mm});
            skPoint(sketch, "E22.18.0", {"position": v(3.3, 4.27) * mm});
            skPoint(sketch, "E22.18.1", {"position": v(3.53, 4.85) * mm});
            skArc(sketch, "E22.18.2", {"start": v(3.64, 5.43) * mm, "mid": v(3.53, 4.88) * mm, "end": v(3.34, 4.36) * mm});
            skArc(sketch, "E22.18.3", {"start": v(3.3, 5.71) * mm, "mid": v(3.45, 5.63) * mm, "end": v(3.59, 5.54) * mm});
            skPoint(sketch, "E22.18.4", {"position": v(3.65, 5.5) * mm});
            skPoint(sketch, "E22.18.5", {"position": v(2.3, 4.88) * mm});
            skArc(sketch, "E22.18.6", {"start": v(3.18, 5.7) * mm, "mid": v(2.74, 5.36) * mm, "end": v(2.36, 4.96) * mm});
            skPoint(sketch, "E22.18.7", {"position": v(3.24, 5.75) * mm});
            skArc(sketch, "E22.18.8", {"start": v(3.34, 4.36) * mm, "mid": v(3.34, 4.28) * mm, "end": v(3.38, 4.21) * mm});
            skArc(sketch, "E22.18.9", {"start": v(3.3, 5.71) * mm, "mid": v(3.24, 5.73) * mm, "end": v(3.18, 5.7) * mm});
            skArc(sketch, "E22.18.10", {"start": v(2.22, 4.92) * mm, "mid": v(2.3, 4.92) * mm, "end": v(2.36, 4.96) * mm});
            skArc(sketch, "E22.18.11", {"start": v(3.64, 5.43) * mm, "mid": v(3.63, 5.5) * mm, "end": v(3.59, 5.54) * mm});
            skPoint(sketch, "E22.19.0", {"position": v(1.82, 5.08) * mm});
            skPoint(sketch, "E22.19.1", {"position": v(1.85, 5.7) * mm});
            skArc(sketch, "E22.19.2", {"start": v(1.79, 6.28) * mm, "mid": v(1.85, 5.73) * mm, "end": v(1.83, 5.18) * mm});
            skArc(sketch, "E22.19.3", {"start": v(1.38, 6.45) * mm, "mid": v(1.54, 6.42) * mm, "end": v(1.7, 6.38) * mm});
            skPoint(sketch, "E22.19.4", {"position": v(1.77, 6.36) * mm});
            skPoint(sketch, "E22.19.5", {"position": v(0.68, 5.36) * mm});
            skArc(sketch, "E22.19.6", {"start": v(1.26, 6.41) * mm, "mid": v(0.95, 5.95) * mm, "end": v(0.72, 5.44) * mm});
            skPoint(sketch, "E22.19.7", {"position": v(1.3, 6.47) * mm});
            skArc(sketch, "E22.19.8", {"start": v(1.83, 5.18) * mm, "mid": v(1.85, 5.1) * mm, "end": v(1.91, 5.05) * mm});
            skArc(sketch, "E22.19.9", {"start": v(1.38, 6.45) * mm, "mid": v(1.31, 6.45) * mm, "end": v(1.26, 6.41) * mm});
            skArc(sketch, "E22.19.10", {"start": v(0.6, 5.37) * mm, "mid": v(0.67, 5.38) * mm, "end": v(0.72, 5.44) * mm});
            skArc(sketch, "E22.19.11", {"start": v(1.79, 6.28) * mm, "mid": v(1.76, 6.34) * mm, "end": v(1.7, 6.38) * mm});
            skSolve(sketch);
        }
        {
            var Q0;
            Q0=qSketchRegion(id+"F0",true);
            extrude(context, id + "F1", {"entities" : qUnion([Q0]), "depth" : 4.8 * mm});
        }
        {
            var Q0;
            Q0=makeQuery(id+"F1.opExtrude","CAP_FACE",FACE,{"disambiguationData":[OSD([sQuery(id+"F0.wireOp",EDGE,"E13"),sQuery(id+"F0.wireOp",EDGE,"E14.MirrorCS"),sQuery(id+"F0.wireOp",EDGE,"E15"),sQuery(id+"F0.wireOp",EDGE,"E16"),sQuery(id+"F0.wireOp",EDGE,"E17.filletArc"),sQuery(id+"F0.wireOp",EDGE,"E18.filletArc"),sQuery(id+"F0.wireOp",EDGE,"E19.filletArc"),sQuery(id+"F0.wireOp",EDGE,"E20.filletArc"),sQuery(id+"F0.wireOp",EDGE,"E22.1.2"),sQuery(id+"F0.wireOp",EDGE,"E22.1.3"),sQuery(id+"F0.wireOp",EDGE,"E22.1.6"),sQuery(id+"F0.wireOp",EDGE,"E22.1.8"),sQuery(id+"F0.wireOp",EDGE,"E22.1.9"),sQuery(id+"F0.wireOp",EDGE,"E22.1.10"),sQuery(id+"F0.wireOp",EDGE,"E22.1.11"),sQuery(id+"F0.wireOp",EDGE,"E22.2.2"),sQuery(id+"F0.wireOp",EDGE,"E22.2.3"),sQuery(id+"F0.wireOp",EDGE,"E22.2.6"),sQuery(id+"F0.wireOp",EDGE,"E22.2.8"),sQuery(id+"F0.wireOp",EDGE,"E22.2.9"),sQuery(id+"F0.wireOp",EDGE,"E22.2.10"),sQuery(id+"F0.wireOp",EDGE,"E22.2.11"),sQuery(id+"F0.wireOp",EDGE,"E22.3.2"),sQuery(id+"F0.wireOp",EDGE,"E22.3.3"),sQuery(id+"F0.wireOp",EDGE,"E22.3.6"),sQuery(id+"F0.wireOp",EDGE,"E22.3.8"),sQuery(id+"F0.wireOp",EDGE,"E22.3.9"),sQuery(id+"F0.wireOp",EDGE,"E22.3.10"),sQuery(id+"F0.wireOp",EDGE,"E22.3.11"),sQuery(id+"F0.wireOp",EDGE,"E22.4.2"),sQuery(id+"F0.wireOp",EDGE,"E22.4.3"),sQuery(id+"F0.wireOp",EDGE,"E22.4.6"),sQuery(id+"F0.wireOp",EDGE,"E22.4.8"),sQuery(id+"F0.wireOp",EDGE,"E22.4.9"),sQuery(id+"F0.wireOp",EDGE,"E22.4.10"),sQuery(id+"F0.wireOp",EDGE,"E22.4.11"),sQuery(id+"F0.wireOp",EDGE,"E22.5.2"),sQuery(id+"F0.wireOp",EDGE,"E22.5.3"),sQuery(id+"F0.wireOp",EDGE,"E22.5.6"),sQuery(id+"F0.wireOp",EDGE,"E22.5.8"),sQuery(id+"F0.wireOp",EDGE,"E22.5.9"),sQuery(id+"F0.wireOp",EDGE,"E22.5.10"),sQuery(id+"F0.wireOp",EDGE,"E22.5.11"),sQuery(id+"F0.wireOp",EDGE,"E22.6.2"),sQuery(id+"F0.wireOp",EDGE,"E22.6.3"),sQuery(id+"F0.wireOp",EDGE,"E22.6.6"),sQuery(id+"F0.wireOp",EDGE,"E22.6.8"),sQuery(id+"F0.wireOp",EDGE,"E22.6.9"),sQuery(id+"F0.wireOp",EDGE,"E22.6.10"),sQuery(id+"F0.wireOp",EDGE,"E22.6.11"),sQuery(id+"F0.wireOp",EDGE,"E22.7.2"),sQuery(id+"F0.wireOp",EDGE,"E22.7.3"),sQuery(id+"F0.wireOp",EDGE,"E22.7.6"),sQuery(id+"F0.wireOp",EDGE,"E22.7.8"),sQuery(id+"F0.wireOp",EDGE,"E22.7.9"),sQuery(id+"F0.wireOp",EDGE,"E22.7.10"),sQuery(id+"F0.wireOp",EDGE,"E22.7.11"),sQuery(id+"F0.wireOp",EDGE,"E22.8.2"),sQuery(id+"F0.wireOp",EDGE,"E22.8.3"),sQuery(id+"F0.wireOp",EDGE,"E22.8.6"),sQuery(id+"F0.wireOp",EDGE,"E22.8.8"),sQuery(id+"F0.wireOp",EDGE,"E22.8.9"),sQuery(id+"F0.wireOp",EDGE,"E22.8.10"),sQuery(id+"F0.wireOp",EDGE,"E22.8.11"),sQuery(id+"F0.wireOp",EDGE,"E22.9.2"),sQuery(id+"F0.wireOp",EDGE,"E22.9.3"),sQuery(id+"F0.wireOp",EDGE,"E22.9.6"),sQuery(id+"F0.wireOp",EDGE,"E22.9.8"),sQuery(id+"F0.wireOp",EDGE,"E22.9.9"),sQuery(id+"F0.wireOp",EDGE,"E22.9.10"),sQuery(id+"F0.wireOp",EDGE,"E22.9.11"),sQuery(id+"F0.wireOp",EDGE,"E22.10.2"),sQuery(id+"F0.wireOp",EDGE,"E22.10.3"),sQuery(id+"F0.wireOp",EDGE,"E22.10.6"),sQuery(id+"F0.wireOp",EDGE,"E22.10.8"),sQuery(id+"F0.wireOp",EDGE,"E22.10.9"),sQuery(id+"F0.wireOp",EDGE,"E22.10.10"),sQuery(id+"F0.wireOp",EDGE,"E22.10.11"),sQuery(id+"F0.wireOp",EDGE,"E22.11.2"),sQuery(id+"F0.wireOp",EDGE,"E22.11.3"),sQuery(id+"F0.wireOp",EDGE,"E22.11.6"),sQuery(id+"F0.wireOp",EDGE,"E22.11.8"),sQuery(id+"F0.wireOp",EDGE,"E22.11.9"),sQuery(id+"F0.wireOp",EDGE,"E22.11.10"),sQuery(id+"F0.wireOp",EDGE,"E22.11.11"),sQuery(id+"F0.wireOp",EDGE,"E22.12.2"),sQuery(id+"F0.wireOp",EDGE,"E22.12.3"),sQuery(id+"F0.wireOp",EDGE,"E22.12.6"),sQuery(id+"F0.wireOp",EDGE,"E22.12.8"),sQuery(id+"F0.wireOp",EDGE,"E22.12.9"),sQuery(id+"F0.wireOp",EDGE,"E22.12.10"),sQuery(id+"F0.wireOp",EDGE,"E22.12.11"),sQuery(id+"F0.wireOp",EDGE,"E22.13.2"),sQuery(id+"F0.wireOp",EDGE,"E22.13.3"),sQuery(id+"F0.wireOp",EDGE,"E22.13.6"),sQuery(id+"F0.wireOp",EDGE,"E22.13.8"),sQuery(id+"F0.wireOp",EDGE,"E22.13.9"),sQuery(id+"F0.wireOp",EDGE,"E22.13.10"),sQuery(id+"F0.wireOp",EDGE,"E22.13.11"),sQuery(id+"F0.wireOp",EDGE,"E22.14.2"),sQuery(id+"F0.wireOp",EDGE,"E22.14.3"),sQuery(id+"F0.wireOp",EDGE,"E22.14.6"),sQuery(id+"F0.wireOp",EDGE,"E22.14.8"),sQuery(id+"F0.wireOp",EDGE,"E22.14.9"),sQuery(id+"F0.wireOp",EDGE,"E22.14.10"),sQuery(id+"F0.wireOp",EDGE,"E22.14.11"),sQuery(id+"F0.wireOp",EDGE,"E22.15.2"),sQuery(id+"F0.wireOp",EDGE,"E22.15.3"),sQuery(id+"F0.wireOp",EDGE,"E22.15.6"),sQuery(id+"F0.wireOp",EDGE,"E22.15.8"),sQuery(id+"F0.wireOp",EDGE,"E22.15.9"),sQuery(id+"F0.wireOp",EDGE,"E22.15.10"),sQuery(id+"F0.wireOp",EDGE,"E22.15.11"),sQuery(id+"F0.wireOp",EDGE,"E22.16.2"),sQuery(id+"F0.wireOp",EDGE,"E22.16.3"),sQuery(id+"F0.wireOp",EDGE,"E22.16.6"),sQuery(id+"F0.wireOp",EDGE,"E22.16.8"),sQuery(id+"F0.wireOp",EDGE,"E22.16.9"),sQuery(id+"F0.wireOp",EDGE,"E22.16.10"),sQuery(id+"F0.wireOp",EDGE,"E22.16.11"),sQuery(id+"F0.wireOp",EDGE,"E22.17.2"),sQuery(id+"F0.wireOp",EDGE,"E22.17.3"),sQuery(id+"F0.wireOp",EDGE,"E22.17.6"),sQuery(id+"F0.wireOp",EDGE,"E22.17.8"),sQuery(id+"F0.wireOp",EDGE,"E22.17.9"),sQuery(id+"F0.wireOp",EDGE,"E22.17.10"),sQuery(id+"F0.wireOp",EDGE,"E22.17.11"),sQuery(id+"F0.wireOp",EDGE,"E22.18.2"),sQuery(id+"F0.wireOp",EDGE,"E22.18.3"),sQuery(id+"F0.wireOp",EDGE,"E22.18.6"),sQuery(id+"F0.wireOp",EDGE,"E22.18.8"),sQuery(id+"F0.wireOp",EDGE,"E22.18.9"),sQuery(id+"F0.wireOp",EDGE,"E22.18.10"),sQuery(id+"F0.wireOp",EDGE,"E22.18.11"),sQuery(id+"F0.wireOp",EDGE,"E22.19.2"),sQuery(id+"F0.wireOp",EDGE,"E22.19.3"),sQuery(id+"F0.wireOp",EDGE,"E22.19.6"),sQuery(id+"F0.wireOp",EDGE,"E22.19.8"),sQuery(id+"F0.wireOp",EDGE,"E22.19.9"),sQuery(id+"F0.wireOp",EDGE,"E22.19.10"),sQuery(id+"F0.wireOp",EDGE,"E22.19.11")])],"isStart":false});
            var sketch = newSketch(context, id + "F2", { "sketchPlane" : qUnion([Q0])});
            skCircle(sketch, "E23", {"center": v(0, 0) * mm, "radius": 1 * mm});
            skSolve(sketch);
        }
        {
            var Q0;
            Q0=qSketchRegion(id+"F2",true);
            extrude(context, id + "F3", {"entities" : qUnion([Q0]), "operationType" : NewBodyOperationType.REMOVE, "oppositeDirection" : true, "depth" : 25 * mm});
        }
    });
